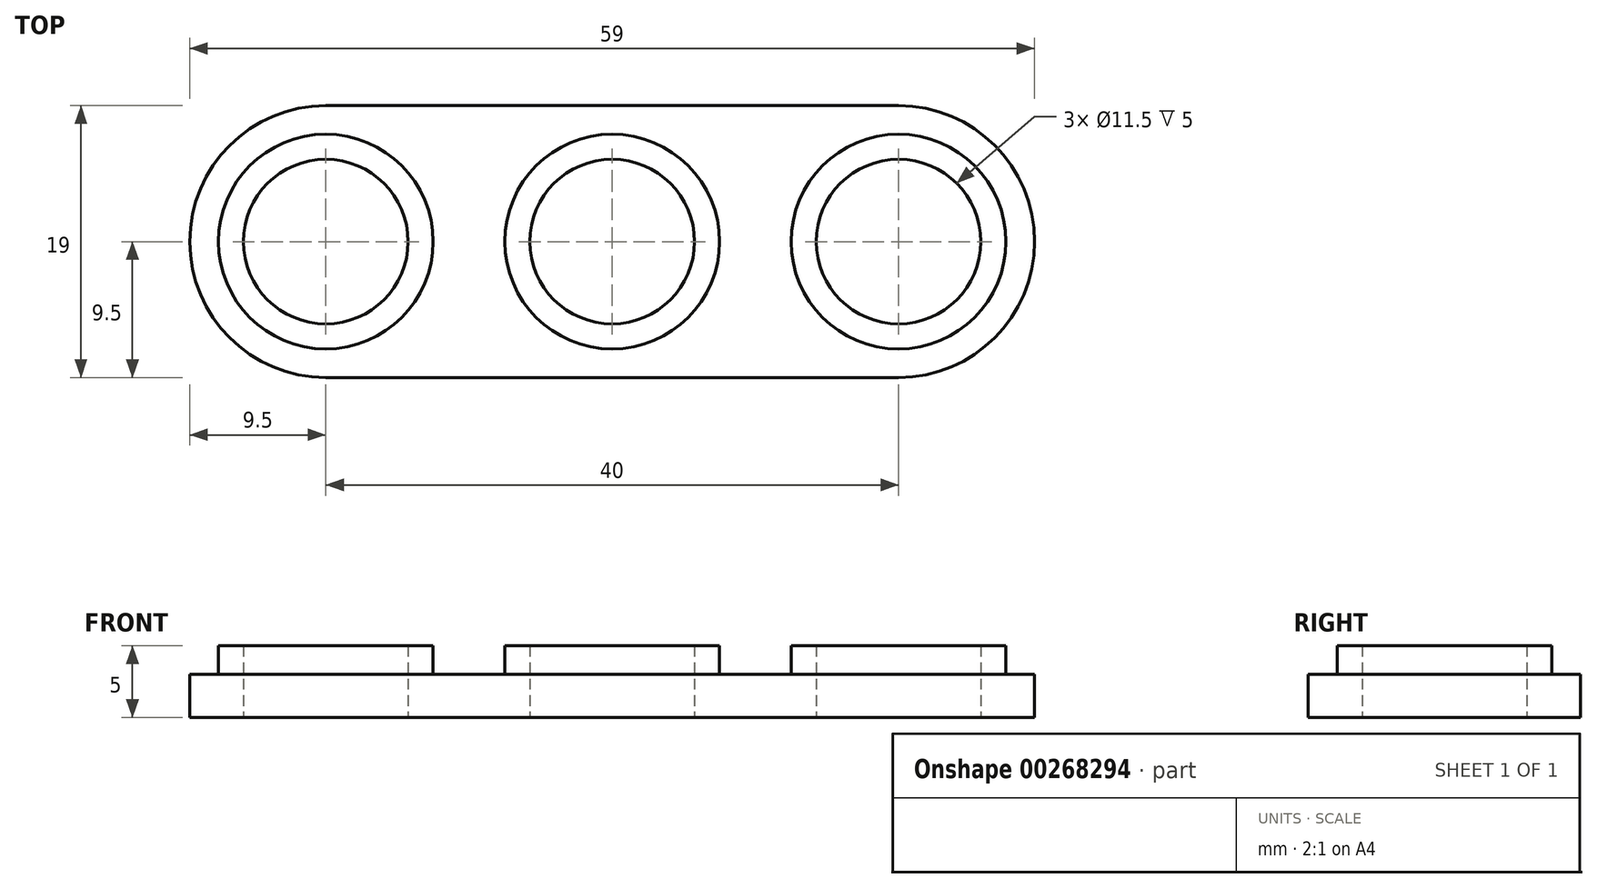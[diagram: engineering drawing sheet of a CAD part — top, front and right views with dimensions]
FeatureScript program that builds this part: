
annotation { "Feature Type Name" : "Feature", "Feature Type Description" : "" }
export const myFeature = defineFeature(function(context is Context, id is Id, definition is map)
    precondition{}
    {
        {
            var Q0;
            Q0=qCreatedBy(makeId("Top.planeOp"),FACE);
            var sketch = newSketch(context, id + "F0", { "sketchPlane" : qUnion([Q0])});
            skLineSegment(sketch, "E0.bottom", {"start": v(0, 9.5) * mm, "end": v(40, 9.5) * mm});
            skLineSegment(sketch, "E0.top", {"start": v(0, -9.5) * mm, "end": v(40, -9.5) * mm});
            skLineSegment(sketch, "E0.left", {"start": v(-9.5, 0) * mm, "end": v(-9.5, 0) * mm});
            skLineSegment(sketch, "E0.right", {"start": v(49.5, 0) * mm, "end": v(49.5, 0) * mm});
            skPoint(sketch, "E1", {"position": v(-9.5, 0) * mm});
            skCircle(sketch, "E2", {"center": v(0, 0) * mm, "radius": 5.75 * mm});
            skPoint(sketch, "E3.visualSharp", {"position": v(49.5, 9.5) * mm});
            skArc(sketch, "E3.filletArc", {"start": v(49.5, 0) * mm, "mid": v(46.72, 6.72) * mm, "end": v(40, 9.5) * mm});
            skPoint(sketch, "E4.visualSharp", {"position": v(49.5, -9.5) * mm});
            skArc(sketch, "E4.filletArc", {"start": v(40, -9.5) * mm, "mid": v(46.72, -6.72) * mm, "end": v(49.5, 0) * mm});
            skPoint(sketch, "E5.visualSharp", {"position": v(-9.5, -9.5) * mm});
            skArc(sketch, "E5.filletArc", {"start": v(-9.5, 0) * mm, "mid": v(-6.72, -6.72) * mm, "end": v(0, -9.5) * mm});
            skPoint(sketch, "E6.visualSharp", {"position": v(-9.5, 9.5) * mm});
            skArc(sketch, "E6.filletArc", {"start": v(0, 9.5) * mm, "mid": v(-6.72, 6.72) * mm, "end": v(-9.5, 0) * mm});
            skCircle(sketch, "E7", {"center": v(0, 0) * mm, "radius": 7.5 * mm});
            skCircle(sketch, "E8.1.0.0", {"center": v(20, 0) * mm, "radius": 5.75 * mm});
            skCircle(sketch, "E8.1.0.1", {"center": v(20, 0) * mm, "radius": 7.5 * mm});
            skCircle(sketch, "E8.2.0.0", {"center": v(40, 0) * mm, "radius": 5.75 * mm});
            skCircle(sketch, "E8.2.0.1", {"center": v(40, 0) * mm, "radius": 7.5 * mm});
            skLineSegment(sketch, "E8.direction1", {"start": v(0, 0) * mm, "end": v(20, 0) * mm, "construction": true});
            skSolve(sketch);
        }
        {
            var Q0;
            Q0=qSketchRegion(id+"F0",true);
            extrude(context, id + "F1", {"entities" : qUnion([Q0]), "depth" : 3 * mm});
        }
        {
            var Q0;
            Q0=makeQuery(id+"F0.imprint","IMPRINT",FACE,{"disambiguationData":[TD([[makeQuery(id+"F0.imprint","IMPRINT",EDGE,{"derivedFrom":sQuery(id+"F0.wireOp",EDGE,"E2")}),-1.0]])]});
            var Q1;
            Q1=makeQuery(id+"F0.imprint","IMPRINT",FACE,{"disambiguationData":[TD([[makeQuery(id+"F0.imprint","IMPRINT",EDGE,{"derivedFrom":sQuery(id+"F0.wireOp",EDGE,"E8.1.0.0")}),-1.0]])]});
            var Q2;
            Q2=makeQuery(id+"F0.imprint","IMPRINT",FACE,{"disambiguationData":[TD([[makeQuery(id+"F0.imprint","IMPRINT",EDGE,{"derivedFrom":sQuery(id+"F0.wireOp",EDGE,"E8.2.0.0")}),-1.0]])]});
            var Q3;
            Q3=makeQuery(id+"F0.imprint","IMPRINT",FACE,{"disambiguationData":[TD([[makeQuery(id+"F0.imprint","IMPRINT",EDGE,{"derivedFrom":sQuery(id+"F0.wireOp",EDGE,"E8.3.0.0")}),-1.0]])]});
            var Q4;
            Q4=makeQuery(id+"F0.imprint","IMPRINT",FACE,{"disambiguationData":[TD([[makeQuery(id+"F0.imprint","IMPRINT",EDGE,{"derivedFrom":sQuery(id+"F0.wireOp",EDGE,"E8.4.0.0")}),-1.0]])]});
            extrude(context, id + "F2", {"entities" : qUnion([Q0, Q1, Q2, Q3, Q4]), "operationType" : NewBodyOperationType.ADD, "depth" : 5 * mm});
        }
    });
